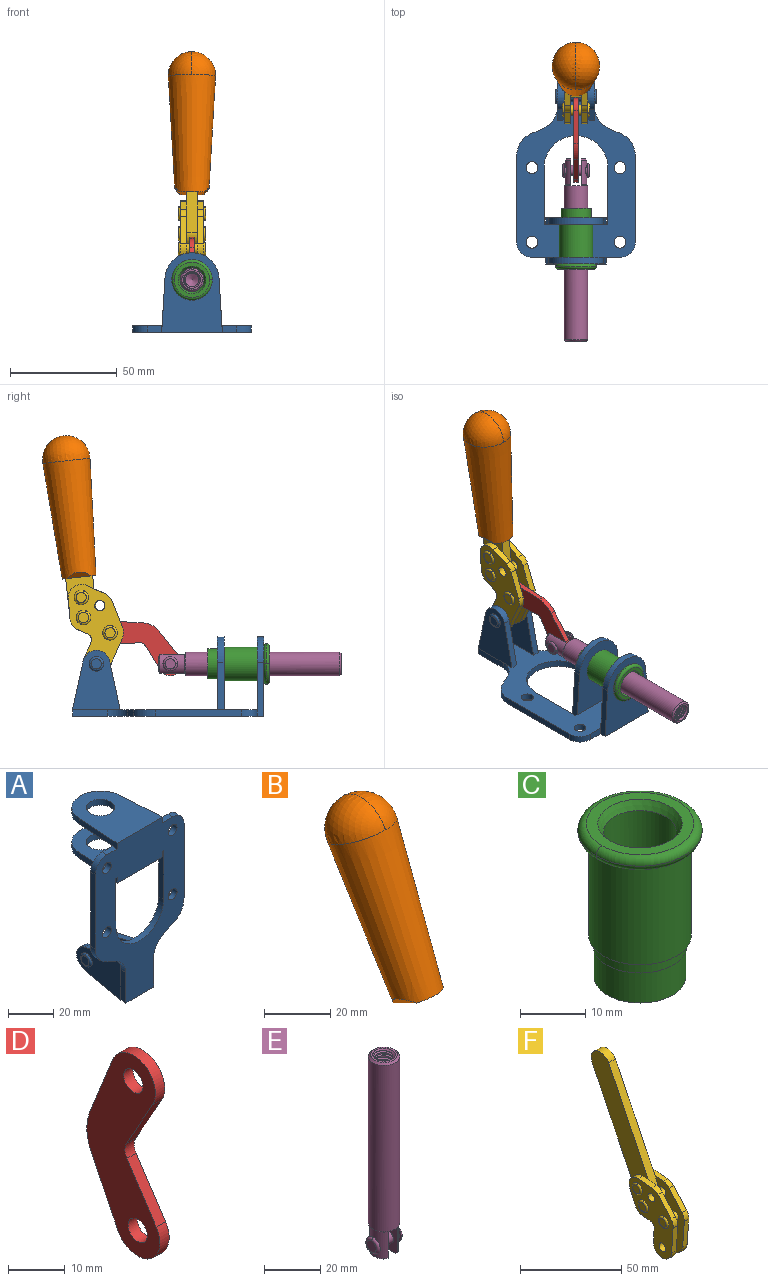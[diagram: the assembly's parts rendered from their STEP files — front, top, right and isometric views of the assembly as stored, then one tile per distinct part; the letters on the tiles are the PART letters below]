
ASSEMBLY  parts=6 mates=6
PART A: 55 faces, bbox 55.7x37.4x89.8 mm
  f0: torus R=2.41mm, axis (-1,0,0), area 15mm2, adj f11,f15,f25
  f1: torus R=2.41mm, axis (-1,0,0), area 15mm2, adj f10,f12,f22
  f2: cylinder r=2.78mm len=5.56mm, axis (0,-1,0), area 54.2mm2, adj f30,f54
  f3: cylinder r=14.99mm len=29.97mm, axis (0,-1,0), area 145.9mm2, adj f30,f49,f53,f54
  f4: cylinder r=2.78mm len=5.56mm, axis (0,-1,0), area 54.2mm2, adj f30,f54
  f5: cylinder r=2.78mm len=5.56mm, axis (0,-1,0), area 54.2mm2, adj f30,f54
  f6: cylinder r=2.78mm len=5.56mm, axis (0,-1,0), area 54.2mm2, adj f30,f54
  f7: cylinder r=6.35mm len=12.7mm, axis (0,0,1), area 123.6mm2, adj f27,f51
  f8: cylinder r=6.35mm len=12.7mm, axis (0,0,-1), area 124.7mm2, adj f21,f35
  f9: cylinder r=2.41mm len=11.18mm, axis (-1,0,0), area 169.4mm2, adj f16,f19
  f10: plane 4.83x4.83mm, normal (1,0,0), area 18.3mm2, adj f1,f12
  f11: plane 4.83x4.83mm, normal (-1,0,0), area 18.3mm2, adj f0,f15
  f12: torus R=2.41mm, axis (-1,0,0), area 15mm2, adj f1,f10,f22
  f13: cylinder r=6.35mm len=12.41mm, axis (1,0,0), area 53.4mm2, adj f18,f19,f22,f23
  f14: cylinder r=6.35mm len=12.41mm, axis (-1,0,0), area 53.4mm2, adj f16,f17,f24,f25
  f15: torus R=2.41mm, axis (-1,0,0), area 15mm2, adj f0,f11,f25
  f16: plane 27.86x22.35mm, normal (1,0,0), area 425.4mm2, adj f9,f14,f17,f24,f30
  f17: plane 22.86x4.97mm, normal (0,0.21,0.98), area 72.5mm2, adj f14,f16,f25,f30
  f18: plane 22.86x4.97mm, normal (0,0.21,0.98), area 72.5mm2, adj f13,f19,f22,f30
  f19: plane 27.86x22.35mm, normal (-1,0,0), area 425.4mm2, adj f9,f13,f18,f23,f30
  f20: cylinder r=12.7mm len=25.35mm, axis (0,0,-1), area 119.8mm2, adj f21,f34,f35,f36
  f21: plane 34.21x28.07mm, normal (0,0,-1), area 702.4mm2, adj f8,f20,f30,f34,f36
  f22: plane 27.96x22.45mm, normal (1,0,0), area 407.2mm2, adj f1,f12,f13,f18,f23,f30,f42,f43
  f23: plane 22.86x4.97mm, normal (0,0.21,-0.98), area 72.5mm2, adj f13,f19,f22,f44
  f24: plane 22.86x4.97mm, normal (0,0.21,-0.98), area 72.5mm2, adj f14,f16,f25,f44
  f25: plane 27.86x22.35mm, normal (-1,0,0), area 407.1mm2, adj f0,f14,f15,f17,f24,f30,f45,f46
  f26: plane 3.1x0.95mm, normal (0,0,-1), area 2.7mm2, adj f30,f49,f50,f54
  f27: plane 34.21x28.07mm, normal (0,0,1), area 702.4mm2, adj f7,f28,f30,f50,f52
  f28: cylinder r=12.7mm len=25.35mm, axis (0,0,1), area 118.8mm2, adj f27,f50,f51,f52
  f29: plane 3.1x0.95mm, normal (0,0,-1), area 2.7mm2, adj f30,f52,f53,f54
  f30: plane 86.54x55.63mm, normal (0,1,0), area 2362.9mm2, adj f2,f3,f4,f5,f6,f16,f17,f18
  f31: plane 40.56x3.1mm, normal (-1,0,0), area 125.7mm2, adj f30,f32,f48,f54
  f32: cylinder r=7.11mm len=7.11mm, axis (0,-1,0), area 34.6mm2, adj f30,f31,f33,f54
  f33: plane 6.67x3.1mm, normal (0,0,1), area 20.4mm2, adj f30,f32,f34,f54
  f34: plane 25.39x3.13mm, normal (-1,0.06,0), area 79.5mm2, adj f20,f21,f33,f35,f54
  f35: plane 37.31x28.45mm, normal (0,0,1), area 789.9mm2, adj f8,f20,f34,f36,f54
  f36: plane 25.39x3.13mm, normal (1,0.06,0), area 79.5mm2, adj f20,f21,f35,f37,f54
  f37: plane 6.67x3.1mm, normal (0,0,1), area 20.4mm2, adj f30,f36,f38,f54
  f38: cylinder r=7.11mm len=7.11mm, axis (0,-1,0), area 34.6mm2, adj f30,f37,f39,f54
  f39: plane 40.56x3.1mm, normal (1,0,0), area 125.7mm2, adj f30,f38,f40,f54
  f40: cylinder r=11.18mm len=10.16mm, axis (0,-1,0), area 39.5mm2, adj f30,f39,f41,f54
  f41: plane 6.09x3.1mm, normal (0.42,0,-0.91), area 20.8mm2, adj f30,f40,f42,f54
  f42: cylinder r=11.18mm len=9.41mm, axis (0,-1,0), area 37.2mm2, adj f22,f30,f41,f43,f54
  f43: plane 16.5x3.1mm, normal (1,0,0), area 51.1mm2, adj f22,f42,f44,f54
  f44: plane 17.37x3.1mm, normal (0,0,-1), area 53.8mm2, adj f23,f24,f30,f43,f45,f54
  f45: plane 16.5x3.1mm, normal (-1,0,0), area 51.1mm2, adj f25,f44,f46,f54
  f46: cylinder r=11.18mm len=9.41mm, axis (0,-1,0), area 37.2mm2, adj f25,f30,f45,f47,f54
  f47: plane 6.09x3.1mm, normal (-0.42,0,-0.91), area 20.8mm2, adj f30,f46,f48,f54
  f48: cylinder r=11.18mm len=10.16mm, axis (0,-1,0), area 39.5mm2, adj f30,f31,f47,f54
  f49: plane 26.54x3.1mm, normal (-1,0,0), area 82.3mm2, adj f3,f26,f30,f54
  f50: plane 25.39x3.1mm, normal (1,0.06,0), area 78.8mm2, adj f26,f27,f28,f51,f54
  f51: plane 37.31x28.45mm, normal (0,0,-1), area 789.9mm2, adj f7,f28,f50,f52,f54
  f52: plane 25.39x3.1mm, normal (-1,0.06,0), area 78.8mm2, adj f27,f28,f29,f51,f54
  f53: plane 26.54x3.1mm, normal (1,0,0), area 82.3mm2, adj f3,f29,f30,f54
  f54: plane 89.66x55.63mm, normal (0,-1,0), area 2678.5mm2, adj f2,f3,f4,f5,f6,f26,f29,f31
PART B: 11 faces, bbox 22.3x42.6x64.5 mm
  f0: sphere r=11.13mm, area 411.4mm2, adj f1,f8
  f1: cone r=11.11mm half-angle=3.3deg, axis (0,0.44,0.9), area 3251.8mm2, adj f0,f7,f8,f9,f10
  f2: cylinder r=6.16mm len=11.7mm, axis (1,0,0), area 89.5mm2, adj f3,f4,f5,f6
  f3: plane 60.23x36.75mm, normal (-1,0,0), area 763.6mm2, adj f2,f4,f6,f10
  f4: plane 51.37x25.05mm, normal (0,0.9,-0.44), area 264.2mm2, adj f2,f3,f5,f10
  f5: plane 60.23x36.75mm, normal (1,0,0), area 763.6mm2, adj f2,f4,f6,f10
  f6: plane 51.37x25.05mm, normal (0,-0.9,0.44), area 264.2mm2, adj f2,f3,f5,f10
  f7: plane 9.95x5.95mm, normal (0.71,-0.31,-0.64), area 25.8mm2, adj f1,f10
  f8: sphere r=11.13mm, area 411.4mm2, adj f0,f1
  f9: plane 9.95x5.95mm, normal (-0.71,-0.31,-0.64), area 25.8mm2, adj f1,f10
  f10: plane 14.27x11.38mm, normal (0,-0.44,-0.9), area 106.7mm2, adj f1,f3,f4,f5,f6,f7,f9
PART C: 15 faces, bbox 20.6x20.6x28.7 mm
  f0: torus R=8.26mm, axis (0,0,1), area 56.8mm2, adj f1,f10,f12
  f1: torus R=8.26mm, axis (0,0,1), area 56.8mm2, adj f0,f6,f13
  f2: cylinder r=5.59mm len=25.91mm, axis (0,0,1), area 909.6mm2, adj f3,f4
  f3: cone r=6.86mm half-angle=45deg, axis (0,0,-1), area 70.2mm2, adj f2,f14
  f4: cone r=6.47mm half-angle=30deg, axis (0,0,1), area 66.7mm2, adj f2,f13
  f5: cylinder r=7.04mm len=14.07mm, axis (0,0,1), area 252.6mm2, adj f11,f14
  f6: torus R=8.26mm, axis (0,0,1), area 56.8mm2, adj f1,f12,f13
  f7: cylinder r=7.16mm len=14.33mm, axis (0,0,1), area 91.5mm2, adj f9,f11
  f8: cylinder r=7.86mm len=18.42mm, axis (0,0,1), area 909.6mm2, adj f9,f10
  f9: plane 15.72x15.72mm, normal (0,0,-1), area 33mm2, adj f7,f8
  f10: plane 16.51x16.51mm, normal (0,0,-1), area 19.9mm2, adj f0,f8,f12
  f11: plane 14.33x14.33mm, normal (0,0,-1), area 5.7mm2, adj f5,f7
  f12: torus R=8.26mm, axis (0,0,1), area 56.8mm2, adj f0,f6,f10
  f13: plane 16.51x16.51mm, normal (0,0,1), area 82.7mm2, adj f1,f4,f6
  f14: plane 14.07x14.07mm, normal (0,0,-1), area 7.8mm2, adj f3,f5
PART D: 12 faces, bbox 2.3x18.2x42.8 mm
  f0: cylinder r=2.4mm len=4.8mm, axis (1,0,0), area 34.9mm2, adj f4,f11
  f1: cylinder r=10.41mm len=8.47mm, axis (1,0,0), area 20.2mm2, adj f4,f9,f10,f11
  f2: cylinder r=3.05mm len=3.16mm, axis (1,0,0), area 7.7mm2, adj f4,f6,f7,f11
  f3: cylinder r=2.4mm len=4.8mm, axis (1,0,0), area 34.9mm2, adj f4,f11
  f4: plane 42.81x18.23mm, normal (-1,0,0), area 414.1mm2, adj f0,f1,f2,f3,f5,f6,f7,f8
  f5: cylinder r=5.54mm len=10.67mm, axis (1,0,0), area 41.8mm2, adj f4,f6,f10,f11
  f6: plane 11.66x6.53mm, normal (0,-0.87,-0.49), area 30.9mm2, adj f2,f4,f5,f11
  f7: plane 11.17x7.33mm, normal (0,-0.84,0.55), area 30.9mm2, adj f2,f4,f8,f11
  f8: cylinder r=5.54mm len=10.51mm, axis (1,0,0), area 41.8mm2, adj f4,f7,f9,f11
  f9: plane 13.67x6.67mm, normal (0,0.9,-0.44), area 35.1mm2, adj f1,f4,f8,f11
  f10: plane 14.1x5.7mm, normal (0,0.93,0.37), area 35.1mm2, adj f1,f4,f5,f11
  f11: plane 42.81x18.23mm, normal (1,0,0), area 414.1mm2, adj f0,f1,f2,f3,f5,f6,f7,f8
PART E: 48 faces, bbox 12.6x11.1x86.1 mm
  f0: torus R=2.41mm, axis (-1,0,0), area 15mm2, adj f30,f32,f34
  f1: torus R=2.41mm, axis (-1,0,0), area 15mm2, adj f29,f31,f33
  f2: cylinder r=5.54mm len=72.39mm, axis (0,0,1), area 2518.5mm2, adj f3,f4,f42,f43
  f3: cone r=5.54mm half-angle=45deg, axis (0,0,1), area 7.6mm2, adj f2,f5,f41
  f4: cone r=5.54mm half-angle=45deg, axis (0,0,-1), area 34.9mm2, adj f2,f39
  f5: cylinder r=5.08mm len=11.48mm, axis (0,0,1), area 108.3mm2, adj f3,f7,f8,f41
  f6: cylinder r=2.41mm len=4.83mm, axis (-1,0,0), area 71.2mm2, adj f40,f41
  f7: cylinder r=2.41mm len=4.83mm, axis (-1,0,0), area 7.6mm2, adj f5,f34
  f8: cone r=5.08mm half-angle=45deg, axis (0,0,1), area 10.6mm2, adj f5,f37,f41
  f9: cone r=3.98mm half-angle=45deg, axis (0,0,1), area 17.6mm2, adj f27,f39,f45,f46,f47
  f10: cylinder r=2.41mm len=4.83mm, axis (-1,0,0), area 7.6mm2, adj f33,f38
  f11: cylinder r=3.2mm len=6.4mm, axis (0,0,1), area 78.4mm2, adj f12,f28,f44,f45,f47
  f12: cylinder r=3.2mm len=6.4mm, axis (0,0,1), area 10.5mm2, adj f11,f13,f45,f47
  f13: cylinder r=3.2mm len=6.4mm, axis (0,0,1), area 10.5mm2, adj f12,f14,f45,f47
  f14: cylinder r=3.2mm len=6.4mm, axis (0,0,1), area 10.5mm2, adj f13,f15,f45,f47
  f15: cylinder r=3.2mm len=6.4mm, axis (0,0,1), area 10.5mm2, adj f14,f16,f45,f47
  f16: cylinder r=3.2mm len=6.4mm, axis (0,0,1), area 10.5mm2, adj f15,f17,f45,f47
  f17: cylinder r=3.2mm len=6.4mm, axis (0,0,1), area 10.5mm2, adj f16,f18,f45,f47
  f18: cylinder r=3.2mm len=6.4mm, axis (0,0,1), area 10.5mm2, adj f17,f19,f45,f47
  f19: cylinder r=3.2mm len=6.4mm, axis (0,0,1), area 10.5mm2, adj f18,f20,f45,f47
  f20: cylinder r=3.2mm len=6.4mm, axis (0,0,1), area 10.5mm2, adj f19,f21,f45,f47
  f21: cylinder r=3.2mm len=6.4mm, axis (0,0,1), area 10.5mm2, adj f20,f22,f45,f47
  f22: cylinder r=3.2mm len=6.4mm, axis (0,0,1), area 10.5mm2, adj f21,f23,f45,f47
  f23: cylinder r=3.2mm len=6.4mm, axis (0,0,1), area 10.5mm2, adj f22,f24,f45,f47
  f24: cylinder r=3.2mm len=6.4mm, axis (0,0,1), area 10.5mm2, adj f23,f25,f45,f47
  f25: cylinder r=3.2mm len=6.4mm, axis (0,0,1), area 10.5mm2, adj f24,f26,f45,f47
  f26: cylinder r=3.2mm len=6.4mm, axis (0,0,1), area 10.5mm2, adj f25,f27,f45,f47
  f27: cylinder r=3.2mm len=6.4mm, axis (0,0,1), area 7.4mm2, adj f9,f26,f45,f47
  f28: cone r=3.2mm half-angle=60deg, axis (0,0,1), area 37.2mm2, adj f11
  f29: plane 4.83x4.83mm, normal (-1,0,0), area 18.3mm2, adj f1,f31
  f30: plane 4.83x4.83mm, normal (1,0,0), area 18.3mm2, adj f0,f32
  f31: torus R=2.41mm, axis (-1,0,0), area 15mm2, adj f1,f29,f33
  f32: torus R=2.41mm, axis (-1,0,0), area 15mm2, adj f0,f30,f34
  f33: plane 6.83x6.83mm, normal (1,0,0), area 18.3mm2, adj f1,f10,f31
  f34: plane 6.83x6.83mm, normal (-1,0,0), area 18.3mm2, adj f0,f7,f32
  f35: cone r=5.08mm half-angle=45deg, axis (0,0,1), area 10.6mm2, adj f36,f38,f40
  f36: plane 7.25x1.97mm, normal (0,0,-1), area 10mm2, adj f35,f40
  f37: plane 7.25x1.97mm, normal (0,0,-1), area 10mm2, adj f8,f41
  f38: cylinder r=5.08mm len=11.48mm, axis (0,0,1), area 108.3mm2, adj f10,f35,f40,f42
  f39: plane 9.55x9.55mm, normal (0,0,1), area 22mm2, adj f4,f9
  f40: plane 12.76x10.09mm, normal (1,0,0), area 95.7mm2, adj f6,f35,f36,f38,f42,f43
  f41: plane 12.76x10.09mm, normal (-1,0,0), area 95.7mm2, adj f3,f5,f6,f8,f37,f43
  f42: cone r=5.54mm half-angle=45deg, axis (0,0,1), area 7.6mm2, adj f2,f38,f40
  f43: plane 11.07x4.7mm, normal (0,0,-1), area 50.4mm2, adj f2,f40,f41
  f44: plane 0.89x0.62mm, normal (-1,0,0), area 0.3mm2, adj f11,f45,f46,f47
  f45: bspline ~24.8x7.63mm, area 266.6mm2, adj f9,f11,f12,f13,f14,f15,f16,f17
  f46: bspline ~24.87x7.63mm, area 73.6mm2, adj f9,f44,f45,f47
  f47: bspline ~24.98x7.63mm, area 272.5mm2, adj f9,f11,f12,f13,f14,f15,f16,f17
PART F: 59 faces, bbox 12.9x60.2x99.6 mm
  f0: torus R=2.39mm, axis (-1,0,0), area 14.9mm2, adj f20,f43,f51
  f1: torus R=2.39mm, axis (-1,0,0), area 14.9mm2, adj f19,f42,f51
  f2: torus R=2.39mm, axis (-1,0,0), area 14.9mm2, adj f18,f35,f51
  f3: torus R=2.39mm, axis (-1,0,0), area 14.9mm2, adj f14,f17,f23
  f4: torus R=2.39mm, axis (-1,0,0), area 14.9mm2, adj f13,f16,f23
  f5: torus R=2.39mm, axis (-1,0,0), area 14.9mm2, adj f12,f15,f23
  f6: cylinder r=2.39mm len=4.78mm, axis (1,0,0), area 46.5mm2, adj f48,f50,f51
  f7: cylinder r=2.39mm len=4.78mm, axis (1,0,0), area 46.5mm2, adj f50,f51
  f8: cylinder r=6.35mm len=12.68mm, axis (1,0,0), area 61.8mm2, adj f38,f39,f50,f51
  f9: cylinder r=2.39mm len=4.78mm, axis (-1,0,0), area 70.5mm2, adj f46,f50
  f10: cylinder r=2.39mm len=4.78mm, axis (-1,0,0), area 46.5mm2, adj f23,f45,f46
  f11: cylinder r=2.39mm len=4.78mm, axis (-1,0,0), area 46.5mm2, adj f23,f46
  f12: plane 4.78x4.78mm, normal (1,0,0), area 17.9mm2, adj f5,f15
  f13: plane 4.78x4.78mm, normal (1,0,0), area 17.9mm2, adj f4,f16
  f14: plane 4.78x4.78mm, normal (1,0,0), area 17.9mm2, adj f3,f17
  f15: torus R=2.39mm, axis (-1,0,0), area 14.9mm2, adj f5,f12,f23
  f16: torus R=2.39mm, axis (-1,0,0), area 14.9mm2, adj f4,f13,f23
  f17: torus R=2.39mm, axis (-1,0,0), area 14.9mm2, adj f3,f14,f23
  f18: plane 4.78x4.78mm, normal (-1,0,0), area 17.9mm2, adj f2,f35
  f19: plane 4.78x4.78mm, normal (-1,0,0), area 17.9mm2, adj f1,f42
  f20: plane 4.78x4.78mm, normal (-1,0,0), area 17.9mm2, adj f0,f43
  f21: plane 2.26x0.2mm, normal (1,0,0), area 0.2mm2, adj f31,f44
  f22: plane 2.26x0.2mm, normal (-1,0,0), area 0.2mm2, adj f41,f44
  f23: plane 39.37x30.77mm, normal (1,0,0), area 565.5mm2, adj f3,f4,f5,f10,f11,f15,f16,f17
  f24: cylinder r=6.1mm len=4.15mm, axis (-1,0,0), area 14.7mm2, adj f23,f25,f32,f46
  f25: plane 10.25x9.01mm, normal (0,-0.75,0.66), area 42.3mm2, adj f23,f24,f26,f46
  f26: cylinder r=6.35mm len=4.64mm, axis (-1,0,0), area 15.6mm2, adj f23,f25,f27,f46
  f27: plane 15.84x3.1mm, normal (0,-1,-0.07), area 49.2mm2, adj f23,f26,f28,f46
  f28: cylinder r=6.35mm len=12.68mm, axis (-1,0,0), area 61.8mm2, adj f23,f27,f29,f46
  f29: plane 8.11x3.1mm, normal (0,1,0.07), area 25.2mm2, adj f23,f28,f30,f46
  f30: cylinder r=3.05mm len=3.25mm, axis (-1,0,0), area 14.8mm2, adj f23,f29,f31,f46
  f31: plane 5.99x3.1mm, normal (0,0.07,-1), area 18.6mm2, adj f21,f23,f30,f44,f46
  f32: plane 9.5x3.1mm, normal (0,-0.07,1), area 29.5mm2, adj f23,f24,f33,f46,f47
  f33: cylinder r=6.1mm len=8.63mm, axis (-1,0,0), area 39.1mm2, adj f23,f32,f34,f47
  f34: plane 8.65x3.96mm, normal (0,0.91,-0.42), area 29.5mm2, adj f23,f33,f44,f47
  f35: torus R=2.39mm, axis (-1,0,0), area 14.9mm2, adj f2,f18,f51
  f36: plane 10.25x9.01mm, normal (0,-0.75,0.66), area 42.3mm2, adj f37,f49,f50,f51
  f37: cylinder r=6.35mm len=4.64mm, axis (1,0,0), area 15.6mm2, adj f36,f38,f50,f51
  f38: plane 15.84x3.1mm, normal (0,-1,-0.07), area 49.2mm2, adj f8,f37,f50,f51
  f39: plane 8.11x3.1mm, normal (0,1,0.07), area 25.2mm2, adj f8,f40,f50,f51
  f40: cylinder r=3.05mm len=3.25mm, axis (1,0,0), area 14.8mm2, adj f39,f41,f50,f51
  f41: plane 5.99x3.1mm, normal (0,0.07,-1), area 18.6mm2, adj f22,f40,f44,f50,f51
  f42: torus R=2.39mm, axis (-1,0,0), area 14.9mm2, adj f1,f19,f51
  f43: torus R=2.39mm, axis (-1,0,0), area 14.9mm2, adj f0,f20,f51
  f44: cylinder r=6.35mm len=12.12mm, axis (-1,0,0), area 128.9mm2, adj f21,f22,f23,f31,f34,f41,f46,f47
  f45: plane 2.65x1.35mm, normal (1,0,0), area 1mm2, adj f10,f55
  f46: plane 39.08x20.42mm, normal (-1,0,0), area 412.5mm2, adj f9,f10,f11,f24,f25,f26,f27,f28
  f47: plane 77.62x39.82mm, normal (1,0,0), area 850mm2, adj f32,f33,f34,f44,f53,f54,f55
  f48: plane 2.65x1.35mm, normal (-1,0,0), area 1mm2, adj f6,f55
  f49: cylinder r=6.1mm len=4.15mm, axis (1,0,0), area 14.7mm2, adj f36,f50,f51,f56
  f50: plane 39.08x20.42mm, normal (1,0,0), area 412.5mm2, adj f6,f7,f8,f9,f36,f37,f38,f39
  f51: plane 39.37x30.77mm, normal (-1,0,0), area 565.5mm2, adj f0,f1,f2,f6,f7,f8,f35,f36
  f52: plane 8.65x3.96mm, normal (0,0.91,-0.42), area 29.5mm2, adj f44,f51,f57,f58
  f53: plane 68.49x33.4mm, normal (0,0.9,-0.44), area 358.1mm2, adj f44,f47,f54,f58
  f54: cylinder r=6.35mm len=12.06mm, axis (1,0,0), area 93.7mm2, adj f47,f53,f55,f58
  f55: plane 68.49x33.4mm, normal (0,-0.9,0.44), area 358.1mm2, adj f44,f45,f46,f47,f48,f50,f54,f58
  f56: plane 9.5x3.1mm, normal (0,-0.07,1), area 29.5mm2, adj f49,f50,f51,f57,f58
  f57: cylinder r=6.1mm len=8.63mm, axis (1,0,0), area 39.1mm2, adj f51,f52,f56,f58
  f58: plane 77.62x39.82mm, normal (-1,0,0), area 850mm2, adj f44,f52,f53,f54,f55,f56,f57
PLACE A rot(axis=(1,0,0),90deg) t=(0,9.43,0)mm fixed
PLACE B rot(axis=(1,0,0),19.8deg) t=(-0.04,7.5,46.48)mm
PLACE C rot(axis=(1,0,0),90deg) t=(0,9.43,0)mm
PLACE D rot(axis=(1,0,0),119.2deg) t=(0,32.41,10.69)mm
PLACE E rot(axis=(1,0,0),90deg) t=(0,22.36,0)mm
PLACE F rot(axis=(1,0,0),19.8deg) t=(0,7.5,46.48)mm
MATE revolute F.f7 <-> A.f0  axis (1,0,0) through (0,41.52,24.61)mm
MATE revolute D.f3 <-> F.f4  axis (1,0,0) through (0,35.12,39.14)mm
MATE fastened C.f2 <-> A.f7  axis (0,1,0) through (0,-36.96,24.61)mm
MATE revolute D.f5 <-> E.f6  axis (1,0,0) through (0,6.89,24.61)mm
MATE slider E.f2 <-> A.f7  axis (0,-1,0) through (0,-36.42,24.61)mm
MATE fastened F.f54 <-> B.f2  axis (1,0,0) through (-2.35,55.8,122.07)mm
